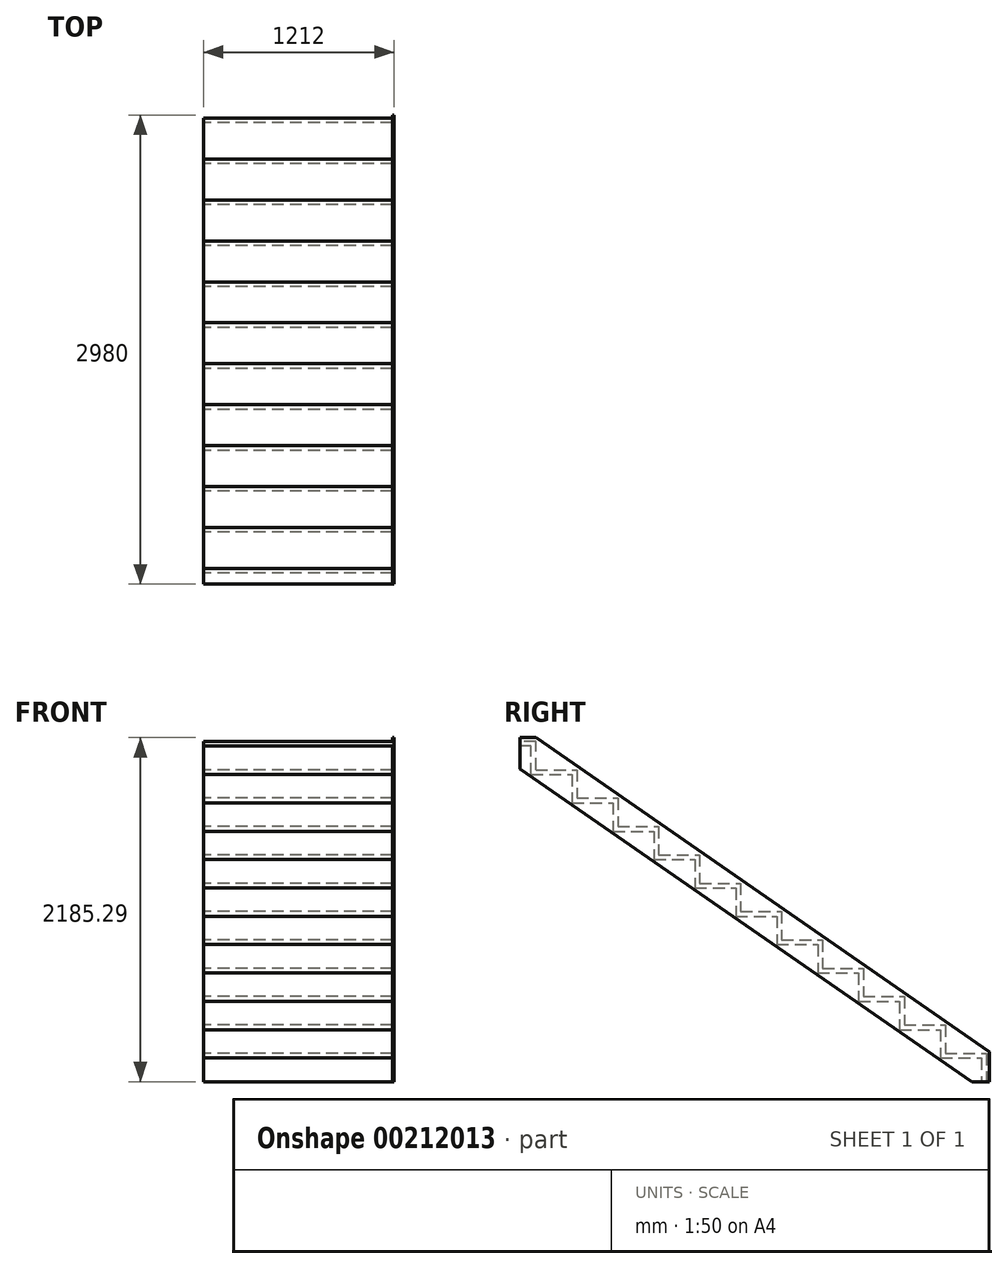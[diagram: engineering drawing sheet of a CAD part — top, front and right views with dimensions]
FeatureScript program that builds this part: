
annotation { "Feature Type Name" : "Feature", "Feature Type Description" : "" }
export const myFeature = defineFeature(function(context is Context, id is Id, definition is map)
    precondition{}
    {
        {
            var Q0;
            Q0=qCreatedBy(makeId("Right.planeOp"),FACE);
            var sketch = newSketch(context, id + "F0", { "sketchPlane" : qUnion([Q0])});
            skLineSegment(sketch, "E0", {"start": v(0, 0) * mm, "end": v(-2960, 0) * mm, "construction": true});
            skLineSegment(sketch, "E1", {"start": v(-2960, 0) * mm, "end": v(-2960, 2160.96) * mm, "construction": true});
            skLineSegment(sketch, "E2", {"start": v(-2860, 1980.88) * mm, "end": v(-2600, 1980.88) * mm});
            skLineSegment(sketch, "E3", {"start": v(-2600, 1980.88) * mm, "end": v(-2600, 1800.8) * mm});
            skLineSegment(sketch, "E4", {"start": v(-2600, 1800.8) * mm, "end": v(-2340, 1800.8) * mm});
            skLineSegment(sketch, "E5", {"start": v(-2340, 1800.8) * mm, "end": v(-2340, 1620.72) * mm});
            skLineSegment(sketch, "E6", {"start": v(-2340, 1620.72) * mm, "end": v(-2080, 1620.72) * mm});
            skLineSegment(sketch, "E7", {"start": v(-2080, 1620.72) * mm, "end": v(-2080, 1440.64) * mm});
            skLineSegment(sketch, "E8", {"start": v(-2080, 1440.64) * mm, "end": v(-1820, 1440.64) * mm});
            skLineSegment(sketch, "E9", {"start": v(-1820, 1440.64) * mm, "end": v(-1820, 1260.56) * mm});
            skLineSegment(sketch, "E10", {"start": v(-1820, 1260.56) * mm, "end": v(-1560, 1260.56) * mm});
            skLineSegment(sketch, "E11", {"start": v(-1560, 1260.56) * mm, "end": v(-1560, 1080.48) * mm});
            skLineSegment(sketch, "E12", {"start": v(-1560, 1080.48) * mm, "end": v(-1300, 1080.48) * mm});
            skLineSegment(sketch, "E13", {"start": v(-1300, 1080.48) * mm, "end": v(-1300, 900.4) * mm});
            skLineSegment(sketch, "E14", {"start": v(-1300, 900.4) * mm, "end": v(-1040, 900.4) * mm});
            skLineSegment(sketch, "E15", {"start": v(-1040, 900.4) * mm, "end": v(-1040, 720.32) * mm});
            skLineSegment(sketch, "E16", {"start": v(-1040, 720.32) * mm, "end": v(-780, 720.32) * mm});
            skLineSegment(sketch, "E17", {"start": v(-780, 720.32) * mm, "end": v(-780, 540.24) * mm});
            skLineSegment(sketch, "E18", {"start": v(-780, 540.24) * mm, "end": v(-520, 540.24) * mm});
            skLineSegment(sketch, "E19", {"start": v(-520, 540.24) * mm, "end": v(-520, 360.16) * mm});
            skLineSegment(sketch, "E20", {"start": v(-520, 360.16) * mm, "end": v(-260, 360.16) * mm});
            skLineSegment(sketch, "E21", {"start": v(-260, 360.16) * mm, "end": v(-260, 180.08) * mm});
            skLineSegment(sketch, "E22", {"start": v(-260, 180.08) * mm, "end": v(0, 180.08) * mm});
            skLineSegment(sketch, "E23", {"start": v(0, 180.08) * mm, "end": v(0, 0) * mm});
            skLineSegment(sketch, "E24", {"start": v(-2860, 1980.88) * mm, "end": v(-2860, 2160.96) * mm});
            skLineSegment(sketch, "E25", {"start": v(-2860, 2160.96) * mm, "end": v(-2960, 2160.96) * mm});
            skPoint(sketch, "E26.orphan", {"position": v(-2960, 1980.88) * mm});
            skLineSegment(sketch, "E27", {"start": v(-2860, 1980.88) * mm, "end": v(-2960, 1980.88) * mm, "construction": true});
            skLineSegment(sketch, "E28.0", {"start": v(-2890, 1950.88) * mm, "end": v(-2890, 2130.96) * mm});
            skLineSegment(sketch, "E29.0", {"start": v(-290, 330.16) * mm, "end": v(-290, 150.08) * mm});
            skLineSegment(sketch, "E29.1", {"start": v(-550, 330.16) * mm, "end": v(-290, 330.16) * mm});
            skLineSegment(sketch, "E29.2", {"start": v(-550, 510.24) * mm, "end": v(-550, 330.16) * mm});
            skLineSegment(sketch, "E29.3", {"start": v(-810, 510.24) * mm, "end": v(-550, 510.24) * mm});
            skLineSegment(sketch, "E29.4", {"start": v(-810, 690.32) * mm, "end": v(-810, 510.24) * mm});
            skLineSegment(sketch, "E29.5", {"start": v(-1070, 690.32) * mm, "end": v(-810, 690.32) * mm});
            skLineSegment(sketch, "E29.6", {"start": v(-1070, 870.4) * mm, "end": v(-1070, 690.32) * mm});
            skLineSegment(sketch, "E29.7", {"start": v(-1330, 870.4) * mm, "end": v(-1070, 870.4) * mm});
            skLineSegment(sketch, "E29.8", {"start": v(-1330, 1050.48) * mm, "end": v(-1330, 870.4) * mm});
            skLineSegment(sketch, "E29.9", {"start": v(-1590, 1050.48) * mm, "end": v(-1330, 1050.48) * mm});
            skLineSegment(sketch, "E29.10", {"start": v(-2370, 1770.8) * mm, "end": v(-2370, 1590.72) * mm});
            skLineSegment(sketch, "E29.11", {"start": v(-2630, 1770.8) * mm, "end": v(-2370, 1770.8) * mm});
            skLineSegment(sketch, "E29.12", {"start": v(-2630, 1950.88) * mm, "end": v(-2630, 1770.8) * mm});
            skLineSegment(sketch, "E29.13", {"start": v(-2890, 1950.88) * mm, "end": v(-2630, 1950.88) * mm});
            skLineSegment(sketch, "E29.14", {"start": v(-2370, 1590.72) * mm, "end": v(-2110, 1590.72) * mm});
            skLineSegment(sketch, "E29.15", {"start": v(-2110, 1590.72) * mm, "end": v(-2110, 1410.64) * mm});
            skLineSegment(sketch, "E29.16", {"start": v(-2110, 1410.64) * mm, "end": v(-1850, 1410.64) * mm});
            skLineSegment(sketch, "E29.17", {"start": v(-1850, 1410.64) * mm, "end": v(-1850, 1230.56) * mm});
            skLineSegment(sketch, "E29.18", {"start": v(-1850, 1230.56) * mm, "end": v(-1590, 1230.56) * mm});
            skLineSegment(sketch, "E29.19", {"start": v(-1590, 1230.56) * mm, "end": v(-1590, 1050.48) * mm});
            skLineSegment(sketch, "E30.0", {"start": v(-290, 150.08) * mm, "end": v(-30, 150.08) * mm});
            skLineSegment(sketch, "E31.0", {"start": v(-30, 150.08) * mm, "end": v(-30, 0) * mm});
            skLineSegment(sketch, "E32", {"start": v(-30, 0) * mm, "end": v(0, 0) * mm});
            skLineSegment(sketch, "E33.0", {"start": v(-2890, 2130.96) * mm, "end": v(-2960, 2130.96) * mm});
            skLineSegment(sketch, "E34", {"start": v(-2960, 2160.96) * mm, "end": v(-2960, 2130.96) * mm});
            skSolve(sketch);
        }
        {
            var Q0;
            Q0 = qSketchRegion(id + "F0", true);
            extrude(context, id + "F1", {"entities" : qUnion([Q0]), "depth" : 1200 * mm});
        }
        {
            var Q0;
            Q0=makeQuery(id+"F1.opExtrude","CAP_FACE",FACE,{"disambiguationData":[OSD([sQuery(id+"F0.wireOp",EDGE,"E2"),sQuery(id+"F0.wireOp",EDGE,"E3"),sQuery(id+"F0.wireOp",EDGE,"E4"),sQuery(id+"F0.wireOp",EDGE,"E5"),sQuery(id+"F0.wireOp",EDGE,"E6"),sQuery(id+"F0.wireOp",EDGE,"E7"),sQuery(id+"F0.wireOp",EDGE,"E8"),sQuery(id+"F0.wireOp",EDGE,"E9"),sQuery(id+"F0.wireOp",EDGE,"E10"),sQuery(id+"F0.wireOp",EDGE,"E11"),sQuery(id+"F0.wireOp",EDGE,"E12"),sQuery(id+"F0.wireOp",EDGE,"E13"),sQuery(id+"F0.wireOp",EDGE,"E14"),sQuery(id+"F0.wireOp",EDGE,"E15"),sQuery(id+"F0.wireOp",EDGE,"E16"),sQuery(id+"F0.wireOp",EDGE,"E17"),sQuery(id+"F0.wireOp",EDGE,"E18"),sQuery(id+"F0.wireOp",EDGE,"E19"),sQuery(id+"F0.wireOp",EDGE,"E20"),sQuery(id+"F0.wireOp",EDGE,"E21"),sQuery(id+"F0.wireOp",EDGE,"E22"),sQuery(id+"F0.wireOp",EDGE,"E23"),sQuery(id+"F0.wireOp",EDGE,"E24"),sQuery(id+"F0.wireOp",EDGE,"E25"),sQuery(id+"F0.wireOp",EDGE,"E28.0"),sQuery(id+"F0.wireOp",EDGE,"E29.0"),sQuery(id+"F0.wireOp",EDGE,"E29.1"),sQuery(id+"F0.wireOp",EDGE,"E29.2"),sQuery(id+"F0.wireOp",EDGE,"E29.3"),sQuery(id+"F0.wireOp",EDGE,"E29.4"),sQuery(id+"F0.wireOp",EDGE,"E29.5"),sQuery(id+"F0.wireOp",EDGE,"E29.6"),sQuery(id+"F0.wireOp",EDGE,"E29.7"),sQuery(id+"F0.wireOp",EDGE,"E29.8"),sQuery(id+"F0.wireOp",EDGE,"E29.9"),sQuery(id+"F0.wireOp",EDGE,"E29.10"),sQuery(id+"F0.wireOp",EDGE,"E29.11"),sQuery(id+"F0.wireOp",EDGE,"E29.12"),sQuery(id+"F0.wireOp",EDGE,"E29.13"),sQuery(id+"F0.wireOp",EDGE,"E29.14"),sQuery(id+"F0.wireOp",EDGE,"E29.15"),sQuery(id+"F0.wireOp",EDGE,"E29.16"),sQuery(id+"F0.wireOp",EDGE,"E29.17"),sQuery(id+"F0.wireOp",EDGE,"E29.18"),sQuery(id+"F0.wireOp",EDGE,"E29.19"),sQuery(id+"F0.wireOp",EDGE,"E30.0"),sQuery(id+"F0.wireOp",EDGE,"E31.0"),sQuery(id+"F0.wireOp",EDGE,"E32"),sQuery(id+"F0.wireOp",EDGE,"E33.0"),sQuery(id+"F0.wireOp",EDGE,"E34")])],"isStart":false});
            var sketch = newSketch(context, id + "F2", { "sketchPlane" : qUnion([Q0])});
            skLineSegment(sketch, "E35", {"start": v(20, 0) * mm, "end": v(-91.26, 0) * mm});
            skLineSegment(sketch, "E36", {"start": v(-91.26, 0) * mm, "end": v(-2960, 1986.93) * mm});
            skLineSegment(sketch, "E37", {"start": v(-2600, 1980.88) * mm, "end": v(-1300, 1080.48) * mm, "construction": true});
            skLineSegment(sketch, "E38", {"start": v(20, 0) * mm, "end": v(20, 190.56) * mm});
            skLineSegment(sketch, "E39", {"start": v(-2960, 2185.29) * mm, "end": v(-2960, 1986.93) * mm});
            skLineSegment(sketch, "E40", {"start": v(-2860, 2185.29) * mm, "end": v(-2960, 2185.29) * mm});
            skLineSegment(sketch, "E41.trimOffspring", {"start": v(-2860, 2185.29) * mm, "end": v(20, 190.56) * mm});
            skLineSegment(sketch, "E42", {"start": v(0, 0) * mm, "end": v(-2960, 0) * mm, "construction": true});
            skLineSegment(sketch, "E43", {"start": v(-2960, 0) * mm, "end": v(-2960, 2160.96) * mm, "construction": true});
            skSolve(sketch);
        }
        {
            var Q0;
            Q0 = qSketchRegion(id + "F2", true);
            extrude(context, id + "F3", {"entities" : qUnion([Q0]), "operationType" : NewBodyOperationType.ADD, "depth" : 12 * mm});
        }
    });
